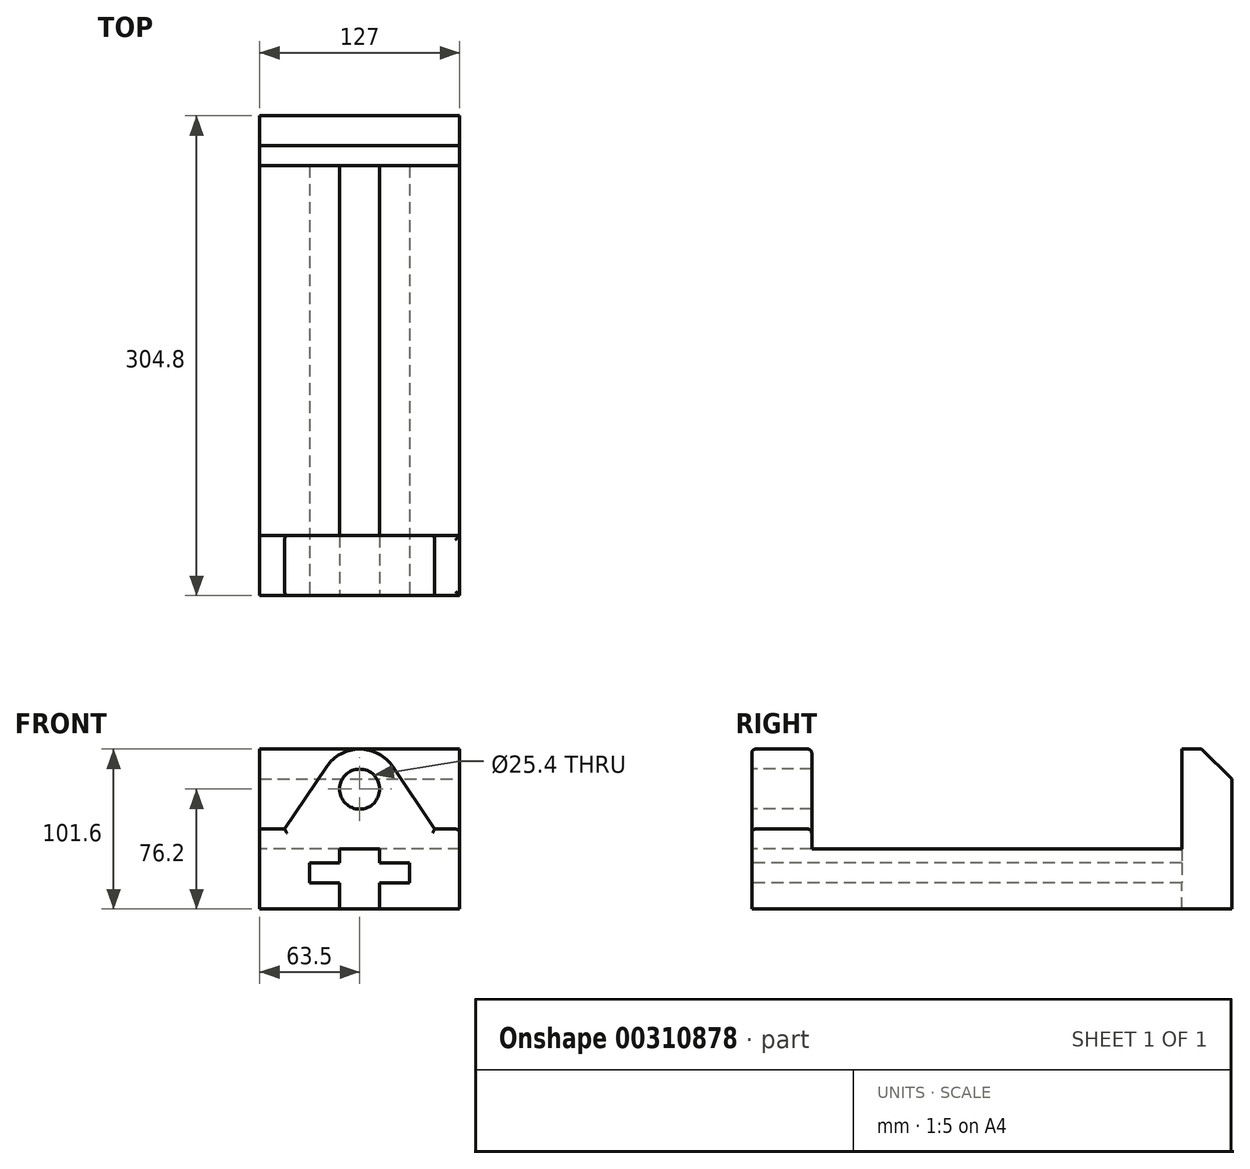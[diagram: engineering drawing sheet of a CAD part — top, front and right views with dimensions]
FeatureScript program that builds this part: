
annotation { "Feature Type Name" : "Feature", "Feature Type Description" : "" }
export const myFeature = defineFeature(function(context is Context, id is Id, definition is map)
    precondition{}
    {
        {
            var Q0;
            Q0=qCreatedBy(makeId("Top.planeOp"),FACE);
            var sketch = newSketch(context, id + "F0", { "sketchPlane" : qUnion([Q0])});
            skLineSegment(sketch, "E0.bottom", {"start": v(63.5, -152.4) * mm, "end": v(-63.5, -152.4) * mm});
            skLineSegment(sketch, "E0.top", {"start": v(63.5, 152.4) * mm, "end": v(-63.5, 152.4) * mm});
            skLineSegment(sketch, "E0.left", {"start": v(63.5, -152.4) * mm, "end": v(63.5, 152.4) * mm});
            skLineSegment(sketch, "E0.right", {"start": v(-63.5, -152.4) * mm, "end": v(-63.5, 152.4) * mm});
            skPoint(sketch, "E0.middle", {"position": v(0, 0) * mm});
            skLineSegment(sketch, "E1", {"start": v(-63.5, 152.4) * mm, "end": v(-63.5, 101.6) * mm});
            skLineSegment(sketch, "E2", {"start": v(-80.4, 101.6) * mm, "end": v(-80.4, 114.3) * mm});
            skLineSegment(sketch, "E3", {"start": v(-80.4, 88.9) * mm, "end": v(-63.5, 88.9) * mm});
            skLineSegment(sketch, "E4", {"start": v(-80.4, 114.3) * mm, "end": v(-63.5, 114.3) * mm});
            skArc(sketch, "E5", {"start": v(-80.4, 114.3) * mm, "mid": v(-93.1, 101.6) * mm, "end": v(-80.4, 88.9) * mm});
            skCircle(sketch, "E6", {"center": v(-80.4, 101.6) * mm, "radius": 1.65 * mm});
            skLineSegment(sketch, "E7", {"start": v(-80.4, 101.6) * mm, "end": v(-64.77, 101.6) * mm});
            skSolve(sketch);
        }
        {
            var Q0;
            Q0=makeQuery(id+"F0.imprint","IMPRINT",FACE,{"disambiguationData":[TD([[makeQuery(id+"F0.imprint","IMPRINT",EDGE,{"derivedFrom":sQuery(id+"F0.wireOp",EDGE,"E0.bottom")}),-1.0]])]});
            extrude(context, id + "F1", {"entities" : qUnion([Q0]), "depth" : 38.1 * mm});
        }
        {
            var Q0;
            Q0=makeQuery(id+"F1.opExtrude","SWEPT_FACE",FACE,{"disambiguationData":[OSD([sQuery(id+"F0.wireOp",EDGE,"E0.bottom")])]});
            var sketch = newSketch(context, id + "F2", { "sketchPlane" : qUnion([Q0])});
            skLineSegment(sketch, "E8", {"start": v(0, 0) * mm, "end": v(12.7, 0) * mm});
            skLineSegment(sketch, "E9", {"start": v(0, 0) * mm, "end": v(-12.7, 0) * mm});
            skLineSegment(sketch, "E10", {"start": v(-12.7, 0) * mm, "end": v(-12.7, 16.51) * mm});
            skLineSegment(sketch, "E11", {"start": v(-12.7, 16.51) * mm, "end": v(-31.75, 16.51) * mm});
            skLineSegment(sketch, "E12", {"start": v(-31.75, 16.51) * mm, "end": v(-31.75, 29.21) * mm});
            skLineSegment(sketch, "E13", {"start": v(-31.75, 29.21) * mm, "end": v(-12.7, 29.21) * mm});
            skLineSegment(sketch, "E14", {"start": v(-12.7, 29.21) * mm, "end": v(-12.7, 38.1) * mm});
            skLineSegment(sketch, "E15", {"start": v(-12.7, 38.1) * mm, "end": v(12.7, 38.1) * mm});
            skLineSegment(sketch, "E16", {"start": v(12.7, 38.1) * mm, "end": v(12.7, 29.21) * mm});
            skLineSegment(sketch, "E17", {"start": v(12.7, 29.21) * mm, "end": v(31.75, 29.21) * mm});
            skLineSegment(sketch, "E18", {"start": v(31.75, 29.21) * mm, "end": v(31.75, 16.51) * mm});
            skLineSegment(sketch, "E19", {"start": v(31.75, 16.51) * mm, "end": v(12.7, 16.51) * mm});
            skLineSegment(sketch, "E20", {"start": v(12.7, 16.51) * mm, "end": v(12.7, 0) * mm});
            skSolve(sketch);
        }
        {
            var Q0;
            Q0=qSketchRegion(id+"F2",true);
            extrude(context, id + "F3", {"entities" : qUnion([Q0]), "operationType" : NewBodyOperationType.REMOVE, "oppositeDirection" : true, "depth" : 273.05 * mm});
        }
        {
            var Q0;
            Q0=makeQuery(id+"F1.opExtrude","CAP_FACE",FACE,{"disambiguationData":[OSD([sQuery(id+"F0.wireOp",EDGE,"E0.bottom"),sQuery(id+"F0.wireOp",EDGE,"E0.top"),sQuery(id+"F0.wireOp",EDGE,"E0.left"),sQuery(id+"F0.wireOp",EDGE,"E0.right")])],"isStart":false});
            var sketch = newSketch(context, id + "F4", { "sketchPlane" : qUnion([Q0])});
            skLineSegment(sketch, "E21.bottom", {"start": v(-63.5, -152.4) * mm, "end": v(63.5, -152.4) * mm});
            skLineSegment(sketch, "E21.top", {"start": v(-63.5, -114.3) * mm, "end": v(63.5, -114.3) * mm});
            skLineSegment(sketch, "E21.left", {"start": v(-63.5, -152.4) * mm, "end": v(-63.5, -114.3) * mm});
            skLineSegment(sketch, "E21.right", {"start": v(63.5, -152.4) * mm, "end": v(63.5, -114.3) * mm});
            skLineSegment(sketch, "E22.top", {"start": v(-63.5, -184.15) * mm, "end": v(63.5, -184.15) * mm});
            skLineSegment(sketch, "E22.left", {"start": v(-63.5, -152.4) * mm, "end": v(-63.5, -184.15) * mm});
            skLineSegment(sketch, "E22.right", {"start": v(63.5, -152.4) * mm, "end": v(63.5, -184.15) * mm});
            skSolve(sketch);
        }
        {
            var Q0;
            {var subQ0=sQuery(id+"F4.wireOp",EDGE,"E21.bottom");var subQ1=sQuery(id+"F2.wireOp",EDGE,"E15");var subQ2=sQuery(id+"F0.wireOp",EDGE,"E0.bottom");var subQ3=makeQuery(id+"F3.boolean.opBoolean","COPY",EDGE,{"derivedFrom":makeQuery(id+"F3.opExtrude","SWEPT_EDGE",EDGE,{"disambiguationData":[OSD([subQ2,sQuery(id+"F2.wireOp",EDGE,"E14"),subQ1])]})});var subQ4=makeQuery(id+"F4.imprint","INTERSECT",VERTEX,{"derivedFrom":[subQ3,subQ0]});var subQ5=makeQuery(id+"F3.boolean.opBoolean","COPY",EDGE,{"derivedFrom":makeQuery(id+"F3.opExtrude","SWEPT_EDGE",EDGE,{"disambiguationData":[OSD([subQ2,subQ1,sQuery(id+"F2.wireOp",EDGE,"E16")])]})});var subQ6=makeQuery(id+"F4.imprint","INTERSECT",VERTEX,{"derivedFrom":[subQ5,subQ0]});Q0=makeQuery(id+"F4.imprint","IMPRINT",FACE,{"disambiguationData":[TD([[makeQuery(id+"F4.imprint","IMPRINT",EDGE,{"disambiguationData":[TD([[subQ4,-1.0],[subQ6,1.0]])],"derivedFrom":subQ0}),1.0]])]});}
            var Q1;
            {var subQ0=sQuery(id+"F4.wireOp",EDGE,"E21.left");Q1=makeQuery(id+"F4.imprint","IMPRINT",FACE,{"disambiguationData":[TD([[makeQuery(id+"F4.imprint","IMPRINT",EDGE,{"derivedFrom":subQ0}),-1.0]])]});}
            var Q2;
            {var subQ0=sQuery(id+"F4.wireOp",EDGE,"E21.right");Q2=makeQuery(id+"F4.imprint","IMPRINT",FACE,{"disambiguationData":[TD([[makeQuery(id+"F4.imprint","IMPRINT",EDGE,{"derivedFrom":subQ0}),1.0]])]});}
            extrude(context, id + "F5", {"entities" : qUnion([Q0, Q1, Q2]), "operationType" : NewBodyOperationType.ADD, "depth" : 12.7 * mm});
        }
        {
            var Q0;
            {var subQ0=sQuery(id+"F0.wireOp",EDGE,"E0.right");var subQ1=sQuery(id+"F0.wireOp",EDGE,"E0.left");var subQ3=sQuery(id+"F0.wireOp",EDGE,"E0.bottom");var subQ6=makeQuery(id+"F1.opExtrude","SWEPT_FACE",FACE,{"disambiguationData":[OSD([subQ3])]});Q0=makeQuery(id+"F5.boolean.opBoolean","MERGE",FACE,{"derivedFrom":[makeQuery(id+"F3.boolean.opBoolean","SPLIT",FACE,{"disambiguationData":[TD([makeQuery(id+"F1.opExtrude","SWEPT_FACE",FACE,{"disambiguationData":[OSD([subQ1])]})])],"derivedFrom":subQ6}),makeQuery(id+"F3.boolean.opBoolean","SPLIT",FACE,{"disambiguationData":[TD([makeQuery(id+"F1.opExtrude","SWEPT_FACE",FACE,{"disambiguationData":[OSD([subQ0])]})])],"derivedFrom":subQ6}),makeQuery(id+"F5.opExtrude","SWEPT_FACE",FACE,{"disambiguationData":[OSD([sQuery(id+"F4.wireOp",EDGE,"E21.bottom")])]})]});}
            var sketch = newSketch(context, id + "F6", { "sketchPlane" : qUnion([Q0])});
            skLineSegment(sketch, "E23", {"start": v(0, 0) * mm, "end": v(0, 76.2) * mm});
            skPoint(sketch, "E23.endSnap0", {"position": v(0, 50.8) * mm});
            skCircle(sketch, "E24", {"center": v(0, 76.2) * mm, "radius": 12.7 * mm});
            skLineSegment(sketch, "E25", {"start": v(-63.5, 50.8) * mm, "end": v(-47.63, 50.8) * mm});
            skLineSegment(sketch, "E26", {"start": v(63.5, 50.8) * mm, "end": v(47.62, 50.8) * mm});
            skLineSegment(sketch, "E27", {"start": v(47.62, 50.8) * mm, "end": v(21.1, 90.35) * mm});
            skLineSegment(sketch, "E28", {"start": v(-47.63, 50.8) * mm, "end": v(-21.1, 90.35) * mm});
            skArc(sketch, "E29", {"start": v(21.1, 90.35) * mm, "mid": v(0, 101.6) * mm, "end": v(-21.1, 90.35) * mm});
            skLineSegment(sketch, "E30", {"start": v(-63.5, 50.8) * mm, "end": v(-63.5, 38.1) * mm});
            skLineSegment(sketch, "E31", {"start": v(-63.5, 38.1) * mm, "end": v(12.7, 38.1) * mm});
            skPoint(sketch, "E31.endSnap0", {"position": v(12.7, 40) * mm});
            skSolve(sketch);
        }
        {
            var Q0;
            Q0=makeQuery(id+"F6.imprint","IMPRINT",FACE,{"disambiguationData":[TD([[makeQuery(id+"F6.imprint","IMPRINT",EDGE,{"derivedFrom":sQuery(id+"F6.wireOp",EDGE,"E24")}),-1.0]])]});
            extrude(context, id + "F7", {"entities" : qUnion([Q0]), "operationType" : NewBodyOperationType.ADD, "oppositeDirection" : true, "depth" : 38.1 * mm});
        }
        {
            var Q0;
            Q0=makeQuery(id+"F5.opExtrude","CAP_EDGE",EDGE,{"disambiguationData":[OSD([sQuery(id+"F4.wireOp",EDGE,"E21.bottom")])],"isStart":false});
            var Q1;
            Q1=makeQuery(id+"F7.opExtrude","CAP_EDGE",EDGE,{"disambiguationData":[OSD([sQuery(id+"F6.wireOp",EDGE,"E27")])],"isStart":true});
            var Q2;
            Q2=makeQuery(id+"F5.opExtrude","CAP_EDGE",EDGE,{"disambiguationData":[OSD([sQuery(id+"F4.wireOp",EDGE,"E21.right")])],"isStart":false});
            var Q3;
            Q3=makeQuery(id+"F5.opExtrude","CAP_EDGE",EDGE,{"disambiguationData":[OSD([sQuery(id+"F4.wireOp",EDGE,"E21.top")])],"isStart":false});
            var Q4;
            Q4=makeQuery(id+"F7.opExtrude","CAP_EDGE",EDGE,{"disambiguationData":[OSD([sQuery(id+"F6.wireOp",EDGE,"E27")])],"isStart":false});
            var Q5;
            Q5=makeQuery(id+"F7.opExtrude","CAP_EDGE",EDGE,{"disambiguationData":[OSD([sQuery(id+"F6.wireOp",EDGE,"E29")])],"isStart":true});
            var Q6;
            Q6=makeQuery(id+"F7.opExtrude","CAP_EDGE",EDGE,{"disambiguationData":[OSD([sQuery(id+"F6.wireOp",EDGE,"E29")])],"isStart":false});
            var Q7;
            Q7=makeQuery(id+"F7.opExtrude","CAP_EDGE",EDGE,{"disambiguationData":[OSD([sQuery(id+"F6.wireOp",EDGE,"E28")])],"isStart":true});
            var Q8;
            Q8=makeQuery(id+"F7.opExtrude","CAP_EDGE",EDGE,{"disambiguationData":[OSD([sQuery(id+"F6.wireOp",EDGE,"E28")])],"isStart":false});
            var Q9;
            Q9=makeQuery(id+"F7.opExtrude","CAP_EDGE",EDGE,{"disambiguationData":[OSD([sQuery(id+"F6.wireOp",EDGE,"E25")])],"isStart":true});
            var Q10;
            Q10=makeQuery(id+"F7.opExtrude","CAP_EDGE",EDGE,{"disambiguationData":[OSD([sQuery(id+"F6.wireOp",EDGE,"E25")])],"isStart":false});
            var Q11;
            Q11=makeQuery(id+"F7.opExtrude","SWEPT_EDGE",EDGE,{"disambiguationData":[OSD([sQuery(id+"F6.wireOp",EDGE,"E25"),sQuery(id+"F6.wireOp",EDGE,"E30")])]});
            fillet(context, id + "F8", {"entities" : qUnion([Q0, Q1, Q2, Q3, Q4, Q5, Q6, Q7, Q8, Q9, Q10, Q11]), "radius" : 2.54 * mm, "tangentPropagation" : true, "allowEdgeOverflow" : false});
        }
        {
            var Q0;
            Q0=makeQuery(id+"F1.opExtrude","CAP_FACE",FACE,{"disambiguationData":[OSD([sQuery(id+"F0.wireOp",EDGE,"E0.bottom"),sQuery(id+"F0.wireOp",EDGE,"E0.top"),sQuery(id+"F0.wireOp",EDGE,"E0.left"),sQuery(id+"F0.wireOp",EDGE,"E0.right"),sQuery(id+"F0.wireOp",EDGE,"E1")])],"isStart":false});
            var sketch = newSketch(context, id + "F9", { "sketchPlane" : qUnion([Q0])});
            skLineSegment(sketch, "E32.bottom", {"start": v(-63.5, 152.4) * mm, "end": v(63.5, 152.4) * mm});
            skLineSegment(sketch, "E32.top", {"start": v(-63.5, 120.65) * mm, "end": v(63.5, 120.65) * mm});
            skLineSegment(sketch, "E32.left", {"start": v(-63.5, 152.4) * mm, "end": v(-63.5, 120.65) * mm});
            skLineSegment(sketch, "E32.right", {"start": v(63.5, 152.4) * mm, "end": v(63.5, 120.65) * mm});
            skSolve(sketch);
        }
        {
            var Q0;
            Q0=makeQuery(id+"F9.imprint","IMPRINT",FACE,{"disambiguationData":[TD([[makeQuery(id+"F9.imprint","IMPRINT",EDGE,{"derivedFrom":sQuery(id+"F9.wireOp",EDGE,"E32.bottom")}),1.0]])]});
            extrude(context, id + "F10", {"entities" : qUnion([Q0]), "operationType" : NewBodyOperationType.ADD, "depth" : 63.5 * mm});
        }
        {
            var Q0;
            Q0=makeQuery(id+"F10.opExtrude","CAP_EDGE",EDGE,{"disambiguationData":[OSD([sQuery(id+"F9.wireOp",EDGE,"E32.bottom")])],"isStart":false});
            chamfer(context, id + "F11", {"entities" : qUnion([Q0]), "width" : 19.05 * mm, "tangentPropagation" : true});
        }
    });
